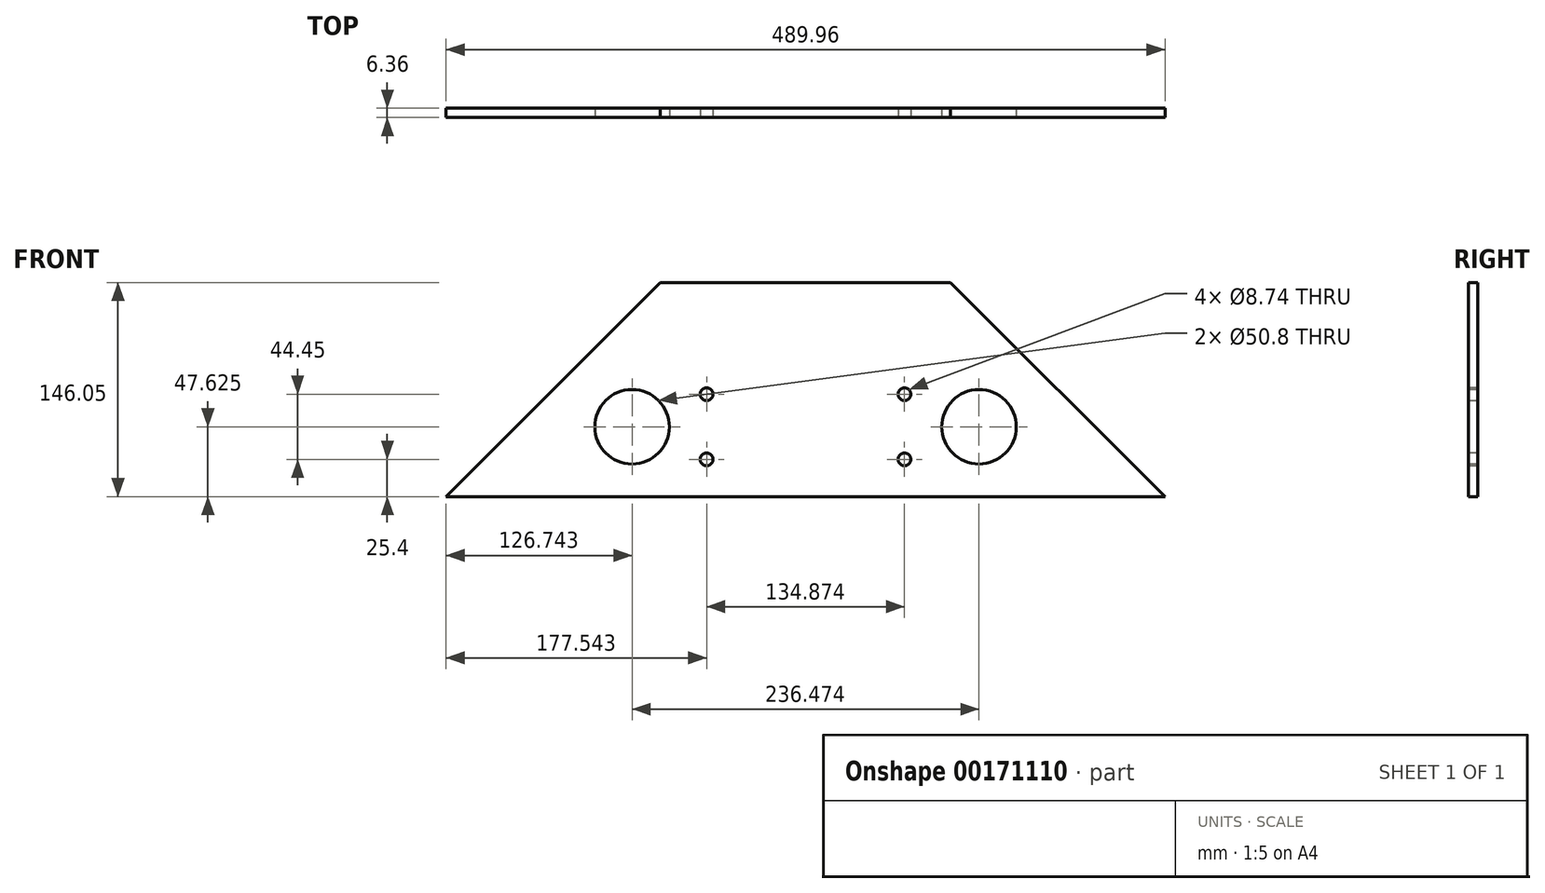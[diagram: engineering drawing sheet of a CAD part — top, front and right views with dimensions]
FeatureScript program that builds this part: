
annotation { "Feature Type Name" : "Feature", "Feature Type Description" : "" }
export const myFeature = defineFeature(function(context is Context, id is Id, definition is map)
    precondition{}
    {
        {
            var Q0;
            Q0=qCreatedBy(makeId("Front.planeOp"),FACE);
            var sketch = newSketch(context, id + "F0", { "sketchPlane" : qUnion([Q0])});
            skLineSegment(sketch, "E0", {"start": v(-98.93, 0) * mm, "end": v(98.93, 0) * mm});
            skLineSegment(sketch, "E1", {"start": v(98.93, 0) * mm, "end": v(244.98, -146.05) * mm});
            skLineSegment(sketch, "E2", {"start": v(244.98, -146.05) * mm, "end": v(-244.98, -146.05) * mm});
            skLineSegment(sketch, "E3", {"start": v(-244.98, -146.05) * mm, "end": v(-98.93, 0) * mm});
            skSolve(sketch);
        }
        {
            var Q0;
            Q0=qSketchRegion(id+"F0",true);
            extrude(context, id + "F1", {"entities" : qUnion([Q0]), "endBound" : BoundingType.SYMMETRIC, "depth" : 6.35 * mm});
        }
        {
            var Q0;
            Q0=makeQuery(id+"F1.opExtrude","CAP_FACE",FACE,{"disambiguationData":[OSD([sQuery(id+"F0.wireOp",EDGE,"E0"),sQuery(id+"F0.wireOp",EDGE,"E1"),sQuery(id+"F0.wireOp",EDGE,"E2"),sQuery(id+"F0.wireOp",EDGE,"E3")])],"isStart":false});
            var sketch = newSketch(context, id + "F2", { "sketchPlane" : qUnion([Q0])});
            skCircle(sketch, "E4", {"center": v(67.44, -76.2) * mm, "radius": 4.37 * mm});
            skCircle(sketch, "E5", {"center": v(67.44, -120.65) * mm, "radius": 4.37 * mm});
            skCircle(sketch, "E6", {"center": v(-67.44, -76.2) * mm, "radius": 4.37 * mm});
            skCircle(sketch, "E7", {"center": v(-67.44, -120.65) * mm, "radius": 4.37 * mm});
            skLineSegment(sketch, "E8", {"start": v(0, 0) * mm, "end": v(0, -146.05) * mm});
            skCircle(sketch, "E9", {"center": v(-118.24, -98.43) * mm, "radius": 25.4 * mm});
            skCircle(sketch, "E10.MirrorC", {"center": v(118.24, -98.42) * mm, "radius": 25.4 * mm});
            skSolve(sketch);
        }
        {
            var Q0;
            Q0 = qSketchRegion(id + "F2", true);
            extrude(context, id + "F3", {"entities" : qUnion([Q0]), "operationType" : NewBodyOperationType.REMOVE, "endBound" : BoundingType.THROUGH_ALL, "oppositeDirection" : true, "depth" : 25.4 * mm});
        }
    });
